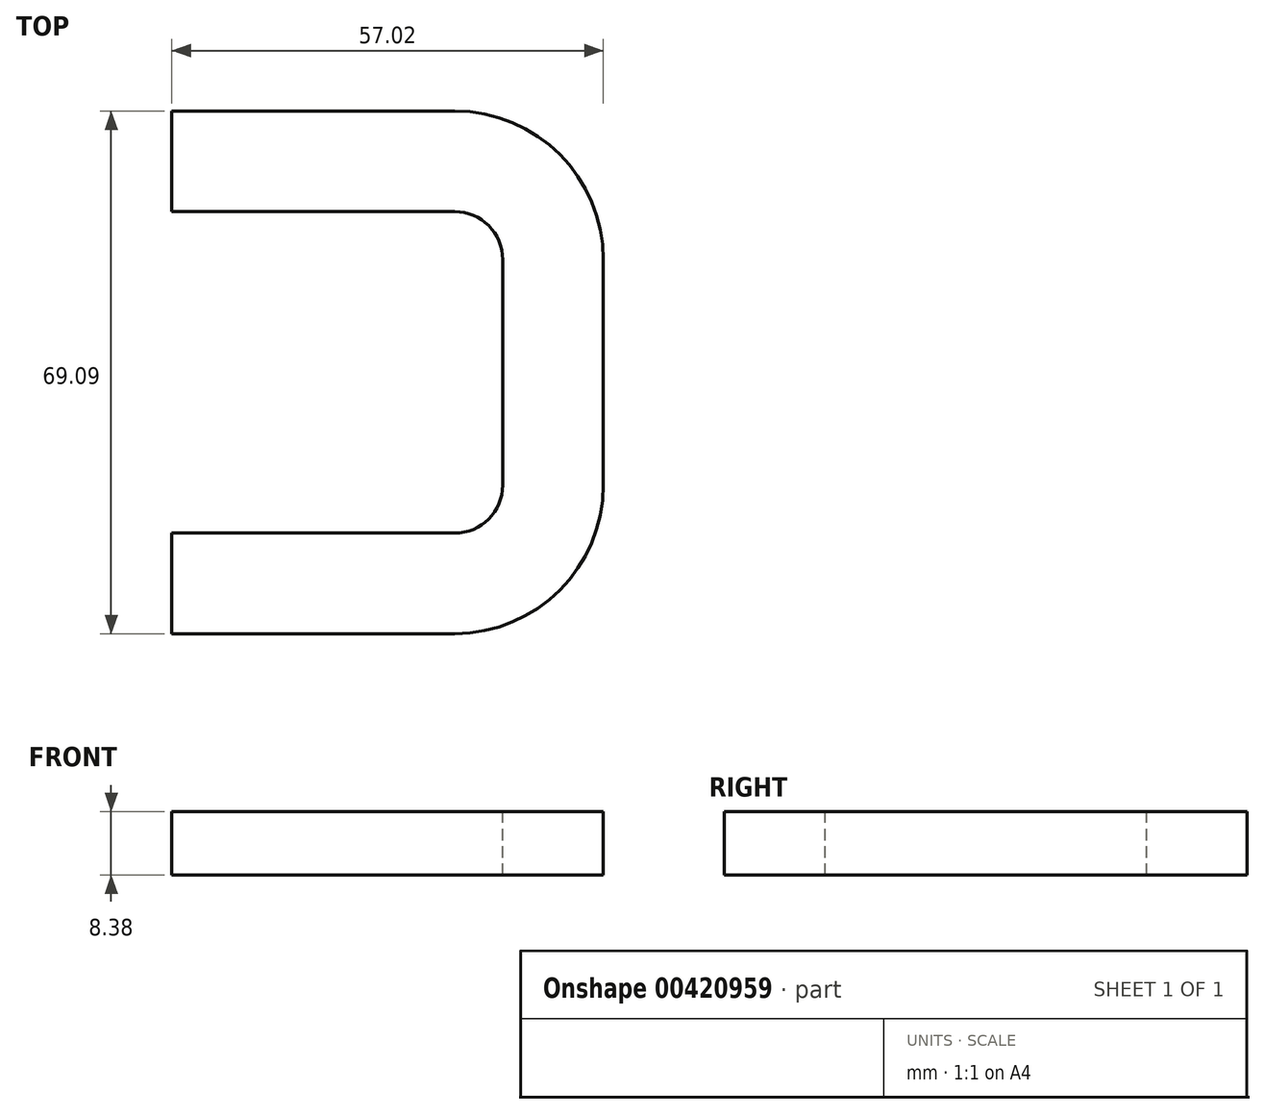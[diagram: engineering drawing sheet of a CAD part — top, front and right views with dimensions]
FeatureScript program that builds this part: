
annotation { "Feature Type Name" : "Feature", "Feature Type Description" : "" }
export const myFeature = defineFeature(function(context is Context, id is Id, definition is map)
    precondition{}
    {
        {
            var Q0;
            Q0=qCreatedBy(makeId("Top.planeOp"),FACE);
            var sketch = newSketch(context, id + "F0", { "sketchPlane" : qUnion([Q0])});
            skLineSegment(sketch, "E0", {"start": v(0, 0) * mm, "end": v(37.38, 0) * mm});
            skLineSegment(sketch, "E1", {"start": v(43.73, -6.35) * mm, "end": v(43.73, -36.15) * mm});
            skLineSegment(sketch, "E2", {"start": v(37.38, -42.5) * mm, "end": v(0, -42.5) * mm});
            skPoint(sketch, "E3.visualSharp", {"position": v(43.73, 0) * mm});
            skArc(sketch, "E3.filletArc", {"start": v(43.73, -6.35) * mm, "mid": v(41.87, -1.86) * mm, "end": v(37.38, 0) * mm});
            skPoint(sketch, "E4.visualSharp", {"position": v(43.73, -42.5) * mm});
            skArc(sketch, "E4.filletArc", {"start": v(37.38, -42.5) * mm, "mid": v(41.87, -40.64) * mm, "end": v(43.73, -36.15) * mm});
            skSolve(sketch);
        }
        {
            var Q0;
            Q0=qCreatedBy(makeId("Right.planeOp"),FACE);
            var sketch = newSketch(context, id + "F1", { "sketchPlane" : qUnion([Q0])});
            skLineSegment(sketch, "E5.bottom", {"start": v(0, 0) * mm, "end": v(13.3, 0) * mm});
            skLineSegment(sketch, "E5.top", {"start": v(0, 8.38) * mm, "end": v(13.3, 8.38) * mm});
            skLineSegment(sketch, "E5.left", {"start": v(0, 0) * mm, "end": v(0, 8.38) * mm});
            skLineSegment(sketch, "E5.right", {"start": v(13.3, 0) * mm, "end": v(13.3, 8.38) * mm});
            skSolve(sketch);
        }
        {
            var Q0;
            Q0=makeQuery(id+"F1.imprint","IMPRINT",FACE,{"disambiguationData":[TD([[makeQuery(id+"F1.imprint","IMPRINT",EDGE,{"derivedFrom":sQuery(id+"F1.wireOp",EDGE,"E5.bottom")}),1.0]])]});
            var Q1;
            Q1=sQuery(id+"F0.wireOp",EDGE,"E0");
            var Q2;
            Q2=sQuery(id+"F0.wireOp",EDGE,"E3.filletArc");
            var Q3;
            Q3=sQuery(id+"F0.wireOp",EDGE,"E1");
            var Q4;
            Q4=sQuery(id+"F0.wireOp",EDGE,"E4.filletArc");
            var Q5;
            Q5=sQuery(id+"F0.wireOp",EDGE,"E2");
            sweep(context, id + "F2", {"profiles" : qUnion([Q0]), "path" : qUnion([Q1, Q2, Q3, Q4, Q5])});
        }
    });
